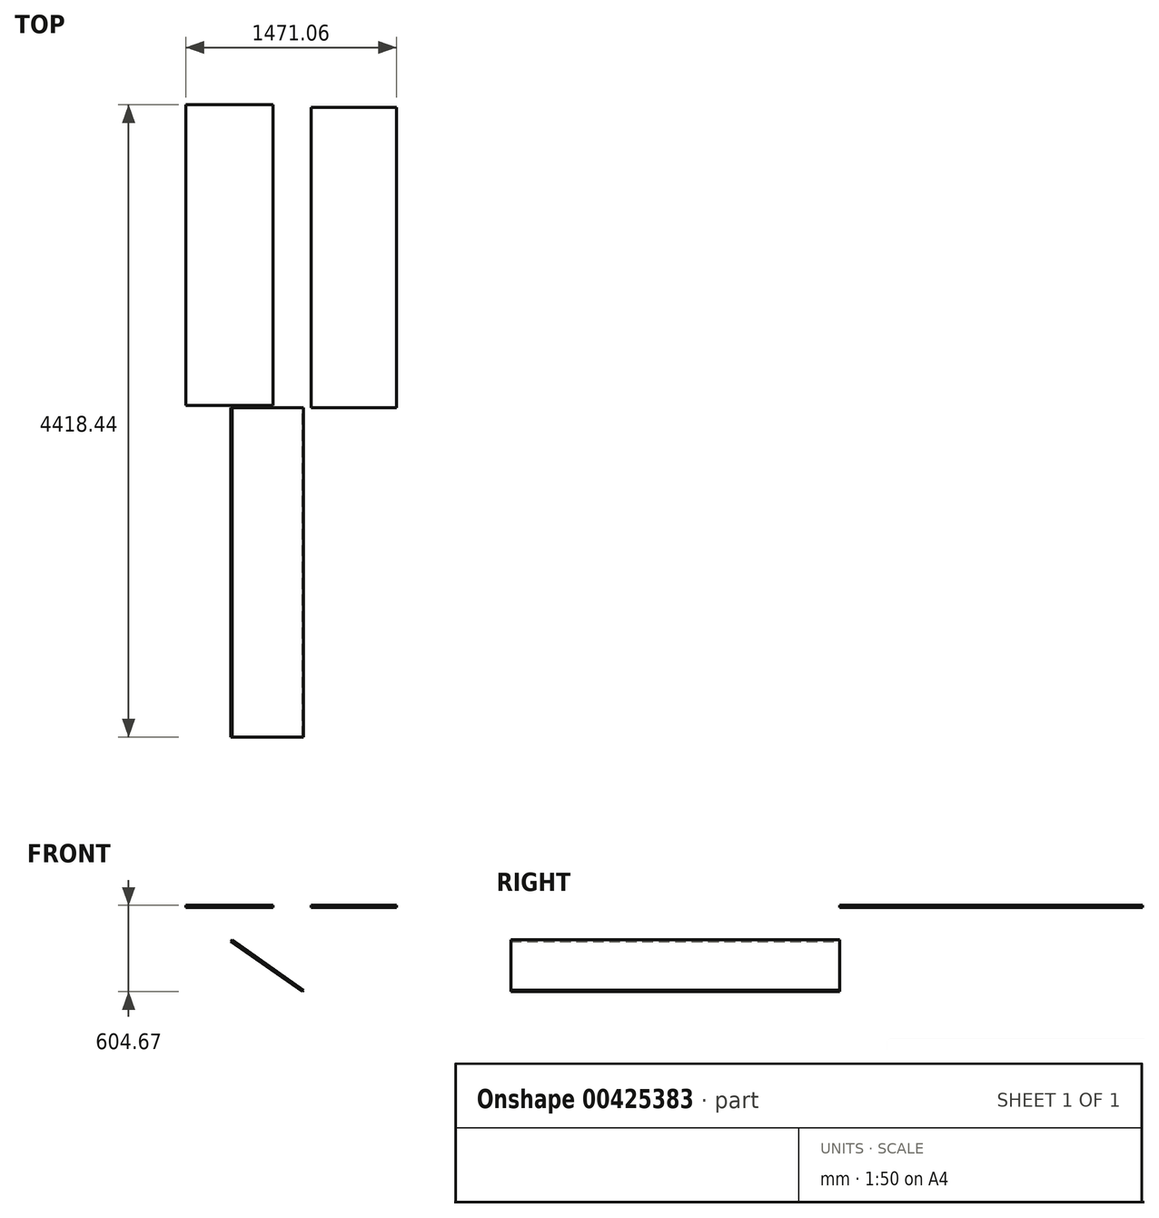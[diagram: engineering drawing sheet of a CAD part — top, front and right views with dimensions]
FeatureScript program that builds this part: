
annotation { "Feature Type Name" : "Feature", "Feature Type Description" : "" }
export const myFeature = defineFeature(function(context is Context, id is Id, definition is map)
    precondition{}
    {
        {
            var Q0;
            Q0=qCreatedBy(makeId("Top.planeOp"),FACE);
            var sketch = newSketch(context, id + "F0", { "sketchPlane" : qUnion([Q0])});
            skLineSegment(sketch, "E0.bottom", {"start": v(-640.8, 2118.44) * mm, "end": v(-30.8, 2118.44) * mm});
            skLineSegment(sketch, "E0.top", {"start": v(-640.8, 18.44) * mm, "end": v(-30.8, 18.44) * mm});
            skLineSegment(sketch, "E0.left", {"start": v(-640.8, 2118.44) * mm, "end": v(-640.8, 18.44) * mm});
            skLineSegment(sketch, "E0.right", {"start": v(-30.8, 2118.44) * mm, "end": v(-30.8, 18.44) * mm});
            skSolve(sketch);
        }
        {
            var Q0;
            Q0=makeQuery(id+"F0.imprint","IMPRINT",FACE,{"disambiguationData":[TD([[makeQuery(id+"F0.imprint","IMPRINT",EDGE,{"derivedFrom":sQuery(id+"F0.wireOp",EDGE,"E0.bottom")}),-1.0]])]});
            extrude(context, id + "F1", {"entities" : qUnion([Q0]), "depth" : 15 * mm});
        }
        {
            var Q0;
            Q0=qCreatedBy(makeId("Top.planeOp"),FACE);
            var sketch = newSketch(context, id + "F2", { "sketchPlane" : qUnion([Q0])});
            skLineSegment(sketch, "E1.bottom", {"start": v(235.25, 0) * mm, "end": v(830.25, 0) * mm});
            skLineSegment(sketch, "E1.top", {"start": v(235.25, 2100) * mm, "end": v(830.25, 2100) * mm});
            skLineSegment(sketch, "E1.left", {"start": v(235.25, 0) * mm, "end": v(235.25, 2100) * mm});
            skLineSegment(sketch, "E1.right", {"start": v(830.25, 0) * mm, "end": v(830.25, 2100) * mm});
            skSolve(sketch);
        }
        {
            var Q0;
            Q0=makeQuery(id+"F2.imprint","IMPRINT",FACE,{"disambiguationData":[TD([[makeQuery(id+"F2.imprint","IMPRINT",EDGE,{"derivedFrom":sQuery(id+"F2.wireOp",EDGE,"E1.bottom")}),1.0]])]});
            extrude(context, id + "F3", {"entities" : qUnion([Q0]), "depth" : 15 * mm});
        }
        {
            var Q0;
            Q0=qCreatedBy(makeId("Front.planeOp"),FACE);
            var sketch = newSketch(context, id + "F4", { "sketchPlane" : qUnion([Q0])});
            skLineSegment(sketch, "E2", {"start": v(173.48, -589.67) * mm, "end": v(-326.2, -239.78) * mm});
            skLineSegment(sketch, "E3", {"start": v(-326.2, -239.78) * mm, "end": v(-317.6, -227.5) * mm});
            skLineSegment(sketch, "E4", {"start": v(173.48, -589.67) * mm, "end": v(182.08, -577.38) * mm});
            skLineSegment(sketch, "E5", {"start": v(182.08, -577.38) * mm, "end": v(-317.6, -227.5) * mm});
            skSolve(sketch);
        }
        {
            var Q0;
            Q0=makeQuery(id+"F4.imprint","IMPRINT",FACE,{"disambiguationData":[TD([[makeQuery(id+"F4.imprint","IMPRINT",EDGE,{"derivedFrom":sQuery(id+"F4.wireOp",EDGE,"E2")}),-1.0]])]});
            extrude(context, id + "F5", {"entities" : qUnion([Q0]), "depth" : 2300 * mm});
        }
    });
